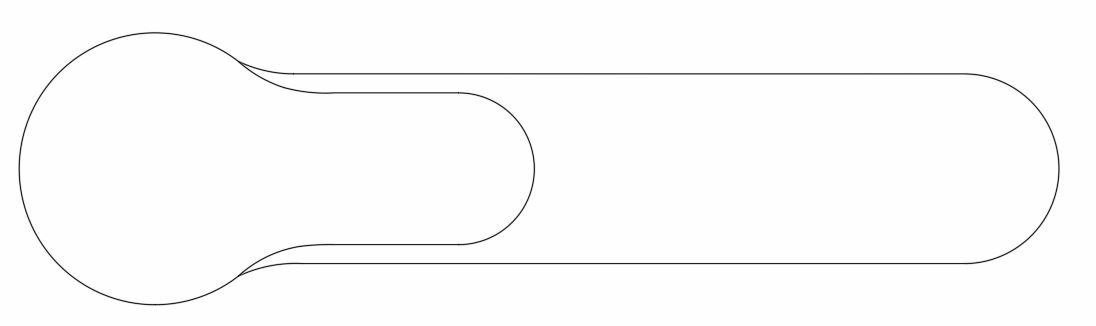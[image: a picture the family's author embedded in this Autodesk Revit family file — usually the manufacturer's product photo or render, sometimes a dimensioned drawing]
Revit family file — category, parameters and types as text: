
# Revit family: Reece_Tap_Roca_L20_Basin Mixer
name_source: partatom
category: Plumbing Fixtures
revit_build: Autodesk Revit 2018 (Build: 20190510_1515(x64)
units: mm (PartAtom-declared; Revit-internal decimal feet)

## family parameters
Cut with Voids When Loaded = No
Host = Face
Part Type = Normal
Room Calculation Point = Yes
Round Connector Dimension = Use Diameter
Shared = Yes

## types (1)
- Chrome
    CWFU = 0
    Default Elevation = 1000 mm  [stored 3.28084 ft]
    Description = Roca L20 Basin Mixer Tap Chrome (4 Star)
    Disclaimer = THIS FILE IS THE PROPERTY OF THE REECE GROUP. IT MAY NOT BE REPRODUCED, REVERSE-ENGINEERED OR MODIFIED. ANY REPUBLICATION, TRANSMISSION OR DISTRIBUTION FOR THE PURPOSE OF COMMERCIALLY EXPLOITING THE FILES IS PROHIBITED.
    HWFU = 0
    Keynote = Product #9504644, Reece_Tap_Roca_L20_Basin Mixer - Chrome
    Manufacturer = Roca
    Model = L20
    Reece_Detail_Disclaimer = THIS FILE IS THE PROPERTY OF THE REECE GROUP. IT MAY NOT BE REPRODUCED, REVERSE-ENGINEERED OR MODIFIED. ANY REPUBLICATION, TRANSMISSION OR DISTRIBUTION FOR THE PURPOSE OF COMMERCIALLY EXPLOITING THE FILES IS PROHIBITED.
    Reece_Detail_Installation = Basin Mixer
    Reece_Material-Main = Reece_Brass_Chrome
    Reece_Overall_Height = 142 mm  [stored 0.465879 ft]
    Reece_Product_Brand = Roca
    Reece_Product_Description = Roca L20 Basin Mixer Tap Chrome (4 Star)
    Reece_Product_Mount = Hob Mounted
    Reece_Product_Number = 9504644
    Reece_Product_Sub Brand = L20
    Reece_Product_Type = Tap
    Reece_Product_Web Page = https://www.reece.com.au
    Reece_Tap_Clearance = 91 mm  [stored 0.298556 ft]
    Reece_Tap_Inlet = 12 mm  [stored 0.0393701 ft]
    Reece_Tap_Reach = 105 mm  [stored 0.344488 ft]
    Type Comments = Tap
    URL = https://www.reece.com.au
    WFU = 0

note: [stored X ft] marks values corroborated as IEEE doubles in the binary element streams (Revit-internal decimal feet)

## geometry (parser evidence)
native form markers: Sweep x2
no freeform markers — native parametric forms only
